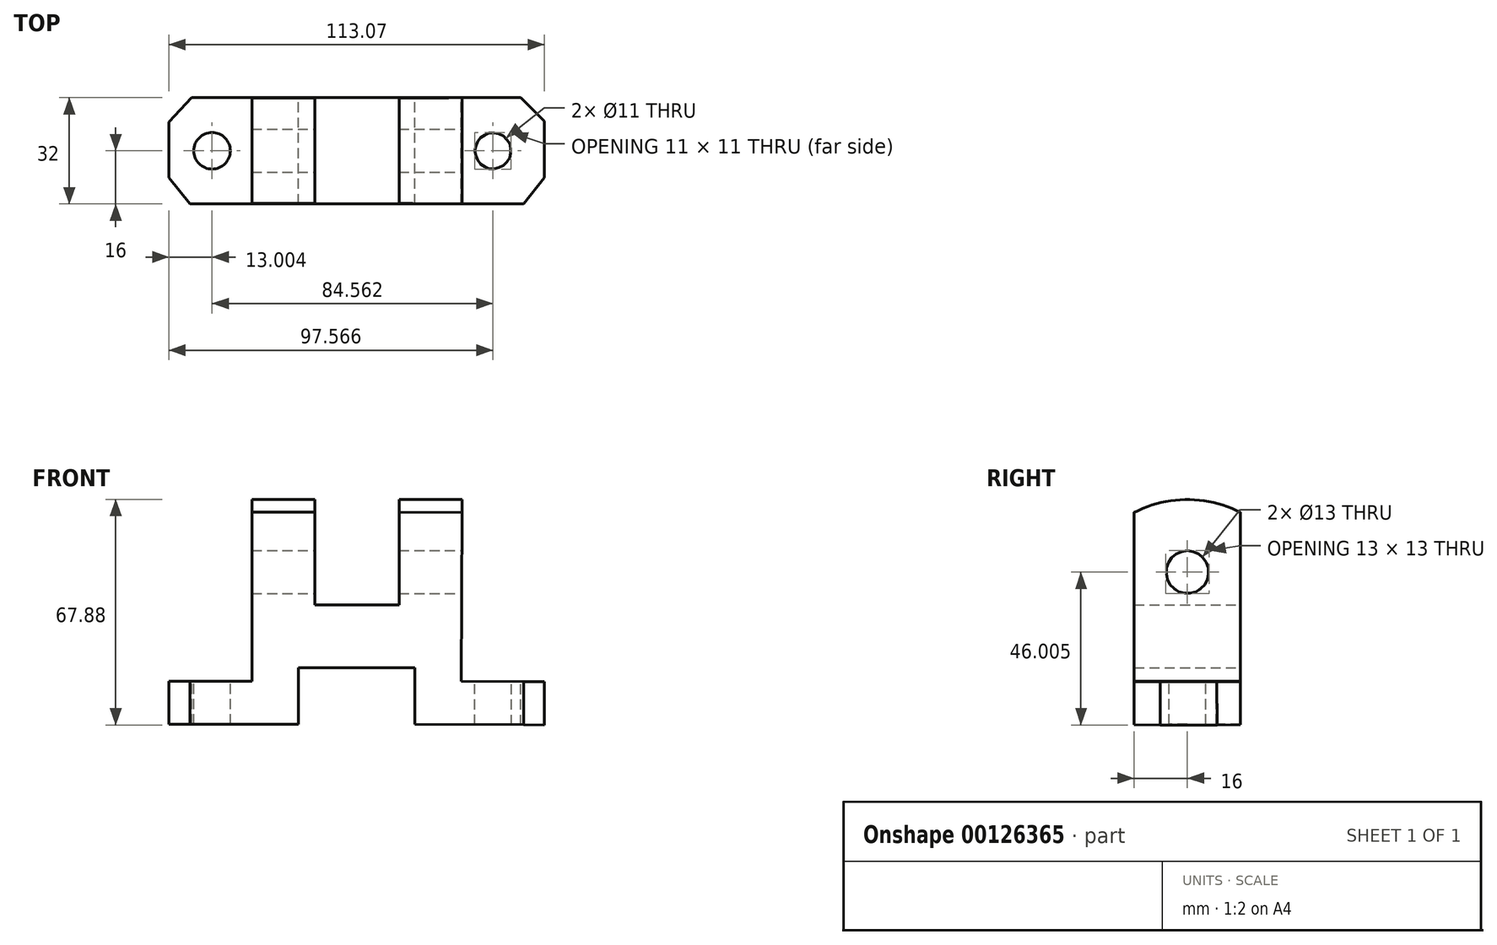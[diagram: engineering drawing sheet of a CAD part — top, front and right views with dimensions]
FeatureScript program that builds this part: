
annotation { "Feature Type Name" : "Feature", "Feature Type Description" : "" }
export const myFeature = defineFeature(function(context is Context, id is Id, definition is map)
    precondition{}
    {
        {
            var Q0;
            Q0=qCreatedBy(makeId("Front.planeOp"),FACE);
            var sketch = newSketch(context, id + "F0", { "sketchPlane" : qUnion([Q0])});
            skLineSegment(sketch, "E0", {"start": v(5.8, -13.55) * mm, "end": v(40.8, -13.55) * mm});
            skLineSegment(sketch, "E1", {"start": v(40.8, -13.55) * mm, "end": v(40.8, -30.55) * mm});
            skLineSegment(sketch, "E2", {"start": v(40.8, -30.55) * mm, "end": v(79.8, -30.74) * mm});
            skLineSegment(sketch, "E3", {"start": v(5.8, -13.55) * mm, "end": v(5.8, -30.55) * mm});
            skLineSegment(sketch, "E4", {"start": v(5.8, -30.55) * mm, "end": v(-33.2, -30.55) * mm});
            skLineSegment(sketch, "E5", {"start": v(-33.2, -30.55) * mm, "end": v(-33.2, -17.55) * mm});
            skLineSegment(sketch, "E6", {"start": v(-33.2, -17.55) * mm, "end": v(-8.2, -17.55) * mm});
            skLineSegment(sketch, "E7", {"start": v(79.8, -30.74) * mm, "end": v(79.87, -17.74) * mm});
            skLineSegment(sketch, "E8", {"start": v(79.87, -17.74) * mm, "end": v(54.87, -17.62) * mm});
            skLineSegment(sketch, "E9", {"start": v(-8.2, -17.55) * mm, "end": v(-8.2, 33.33) * mm});
            skLineSegment(sketch, "E10", {"start": v(54.87, -17.62) * mm, "end": v(55.1, 33.26) * mm});
            skLineSegment(sketch, "E11", {"start": v(-8.2, 33.33) * mm, "end": v(10.8, 33.33) * mm});
            skLineSegment(sketch, "E12", {"start": v(10.8, 33.33) * mm, "end": v(10.8, 5.44) * mm});
            skLineSegment(sketch, "E13", {"start": v(10.8, 5.44) * mm, "end": v(36.1, 5.44) * mm});
            skLineSegment(sketch, "E14", {"start": v(36.1, 5.44) * mm, "end": v(36.1, 33.33) * mm});
            skLineSegment(sketch, "E15", {"start": v(36.1, 33.33) * mm, "end": v(55.1, 33.26) * mm});
            skSolve(sketch);
        }
        {
            var Q0;
            Q0 = qSketchRegion(id + "F0", true);
            extrude(context, id + "F1", {"entities" : qUnion([Q0]), "endBound" : BoundingType.SYMMETRIC, "depth" : 32 * mm});
        }
        {
            var Q0;
            Q0=qCreatedBy(makeId("Right.planeOp"),FACE);
            var sketch = newSketch(context, id + "F2", { "sketchPlane" : qUnion([Q0])});
            skLineSegment(sketch, "E16.0", {"start": v(-16, 33.26) * mm, "end": v(16, 33.26) * mm});
            skCircle(sketch, "E17", {"center": v(0, 15.26) * mm, "radius": 6.5 * mm});
            skSolve(sketch);
        }
        {
            var Q0;
            Q0 = qSketchRegion(id + "F2", true);
            extrude(context, id + "F3", {"entities" : qUnion([Q0]), "operationType" : NewBodyOperationType.REMOVE, "endBound" : BoundingType.SYMMETRIC, "oppositeDirection" : true, "depth" : 200 * mm});
        }
        {
            var Q0;
            Q0=qCreatedBy(makeId("Right.planeOp"),FACE);
            var sketch = newSketch(context, id + "F4", { "sketchPlane" : qUnion([Q0])});
            skLineSegment(sketch, "E18.0", {"start": v(-16, 33.26) * mm, "end": v(16, 33.26) * mm});
            skArc(sketch, "E19", {"start": v(16, 33.26) * mm, "mid": v(0, 37.14) * mm, "end": v(-16, 33.26) * mm});
            skSolve(sketch);
        }
        {
            var Q0;
            Q0 = qSketchRegion(id + "F4", true);
            var Q1;
            Q1=makeQuery(id+"F1.opExtrude","SWEPT_FACE",FACE,{"disambiguationData":[OSD([sQuery(id+"F0.wireOp",EDGE,"E12")])]});
            var Q2;
            Q2=makeQuery(id+"F1.opExtrude","SWEPT_FACE",FACE,{"disambiguationData":[OSD([sQuery(id+"F0.wireOp",EDGE,"E9")])]});
            extrude(context, id + "F5", {"entities" : qUnion([Q0]), "operationType" : NewBodyOperationType.ADD, "endBound" : BoundingType.UP_TO_SURFACE, "endBoundEntityFace" : qUnion([Q1]), "depth" : 11 * mm, "hasSecondDirection" : true, "secondDirectionBound" : SecondDirectionBoundingType.UP_TO_SURFACE, "secondDirectionOppositeDirection" : true, "secondDirectionBoundEntityFace" : qUnion([Q2]), "secondDirectionDepth" : 8 * mm});
        }
        {
            var Q0;
            Q0=qCreatedBy(makeId("Right.planeOp"),FACE);
            var sketch = newSketch(context, id + "F6", { "sketchPlane" : qUnion([Q0])});
            skArc(sketch, "E20.0", {"start": v(16, 33.26) * mm, "mid": v(0, 37.14) * mm, "end": v(-16, 33.26) * mm});
            skLineSegment(sketch, "E20.1", {"start": v(-16, 33.26) * mm, "end": v(16, 33.26) * mm});
            skSolve(sketch);
        }
        {
            var Q0;
            Q0 = qSketchRegion(id + "F6", true);
            var Q1;
            Q1=makeQuery(id+"F1.opExtrude","SWEPT_FACE",FACE,{"disambiguationData":[OSD([sQuery(id+"F0.wireOp",EDGE,"E10")])]});
            var Q2;
            Q2=makeQuery(id+"F1.opExtrude","SWEPT_FACE",FACE,{"disambiguationData":[OSD([sQuery(id+"F0.wireOp",EDGE,"E14")])]});
            extrude(context, id + "F7", {"entities" : qUnion([Q0]), "operationType" : NewBodyOperationType.ADD, "endBound" : BoundingType.UP_TO_SURFACE, "endBoundEntityFace" : qUnion([Q1]), "depth" : 55 * mm, "hasSecondDirection" : true, "secondDirectionBound" : SecondDirectionBoundingType.UP_TO_SURFACE, "secondDirectionOppositeDirection" : false, "secondDirectionBoundEntityFace" : qUnion([Q2]), "secondDirectionDepth" : 36 * mm});
        }
        {
            var Q0;
            Q0=qCreatedBy(makeId("Top.planeOp"),FACE);
            var sketch = newSketch(context, id + "F8", { "sketchPlane" : qUnion([Q0])});
            skCircle(sketch, "E21", {"center": v(-20.2, 0) * mm, "radius": 5.5 * mm});
            skCircle(sketch, "E22", {"center": v(64.37, 0) * mm, "radius": 5.5 * mm});
            skLineSegment(sketch, "E23.0", {"start": v(-33.2, 16) * mm, "end": v(-8.2, 16) * mm});
            skLineSegment(sketch, "E23.1", {"start": v(-33.2, -16) * mm, "end": v(-33.2, 16) * mm});
            skLineSegment(sketch, "E23.2", {"start": v(-33.2, -16) * mm, "end": v(-8.2, -16) * mm});
            skLineSegment(sketch, "E23.3", {"start": v(79.87, -16) * mm, "end": v(54.87, -16) * mm});
            skLineSegment(sketch, "E23.4", {"start": v(79.87, -16) * mm, "end": v(79.87, 16) * mm});
            skLineSegment(sketch, "E23.5", {"start": v(79.87, 16) * mm, "end": v(54.87, 16) * mm});
            skLineSegment(sketch, "E24", {"start": v(-33.2, 8.67) * mm, "end": v(-26.3, 16) * mm});
            skLineSegment(sketch, "E25", {"start": v(-33.2, -8.13) * mm, "end": v(-26.9, -16) * mm});
            skLineSegment(sketch, "E26", {"start": v(72.74, 16) * mm, "end": v(79.87, 8.88) * mm});
            skLineSegment(sketch, "E27", {"start": v(73.58, -16) * mm, "end": v(79.87, -8.13) * mm});
            skSolve(sketch);
        }
        {
            var Q0;
            Q0 = qSketchRegion(id + "F8", true);
            extrude(context, id + "F9", {"entities" : qUnion([Q0]), "operationType" : NewBodyOperationType.REMOVE, "oppositeDirection" : true, "depth" : 100 * mm});
        }
    });
